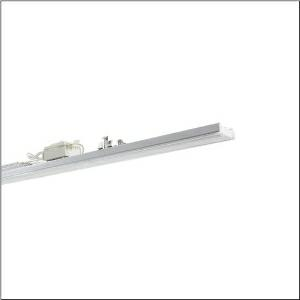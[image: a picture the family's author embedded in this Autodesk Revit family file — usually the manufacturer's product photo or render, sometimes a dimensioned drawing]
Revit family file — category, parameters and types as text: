
# Revit family: licross_r__21_recessed_mo_52tl12dn455g_fe02
name_source: partatom
category: Lighting Fixtures
units: mm (PartAtom-declared; Revit-internal decimal feet)

## family parameters
Cut with Voids When Loaded = No
Host = Face
Light Source = No
Part Type = Normal
Room Calculation Point = No
Round Connector Dimension = Use Diameter
Shared = No

## types (1)
- --- (1 x LED, 5500 lm, 29.6 W, 4000K)
    Apparent Load = 30 VA
    CIE Flux Codes = 72 92 99 100 100
    Color Rendering = 80
    Color Temperature = 4000K
    Default Elevation = 1800 mm
    Description = Licross® 21 Recessed MO, luminaire insert, of sheet steel, galvanised, coil coated, white, length: 1.500mm, width: 66mm, height: 67mm, LED rated luminous flux: 5.500lm, light colour: 840, control gear: DALI 2, with plug, 5-pole, with phase selection, mains connection: 220..240V, AC, 50/60Hz, rated input power: 30W, internal wiring halogen-free, primary optical cover: cover, of PMMA, light emission: direct distribution, primary light characteristic: symmetric, protection rating (complete): IP40, insulation class (complete): insulation class I (protective earthing), certification: CE, ENEC, VDE, UKCA, protection symbol: D if used in an environment without relevant dust loads with corresponding accessories, impact resistance: IK06, permissible ambient temperature for indoor applications: -25..+45°C, corresponds to IFS (International Featured Standards) requirements for safety and quality in the food industry, reducing of maximum allowable ambient temperature of 5°C with ceiling mounting, LABS conformity tested according to VDMA 24364:2018-05, packaging unit: 1 piece
    Height = 58 mm
    Lamp = 1 x LED
    Lamp Light Flux = 5500 lm
    Lamp Power = 29.6 W
    Lamp count = 1
    Length = 1500 mm
    Luminous efficacy = 186 lm/W
    Manufacturer = Siteco
    ModVariant = No
    Model = 52TL12DN455G
    Mounting Place = Ceiling
    Mounting Type = Pendant
    Number of Poles = 1
    OnlyDefault = Yes
    Power Factor = 1
    Product Name = Licross® 21 Recessed MO
    Product group = luminaire insert | ceiling pendant
    ProductGroupID = 902
    Protection Class = Protection class I
    Protection Degree = IP 40
    RLX_Detail_Level = 1
    RLX_Emergency_Light_Flux = 0 lm
    RLX_Emergency_Type = 0
    RLX_Emergency_Type_DB = No
    RlxData = <blob elided: 24037 chars, md5=a2fb8323>
    Socket = socket
    Standby Power = 0 W
    System Light Flux = 5500 lm
    System Power = 30 W
    Type Comments = factory setting: luminous flux: 100 % | dim-lin: 254 | 200 mA
    Type Image = l_1296930.jpg
    URL = http://relux.com
    VarID = @adj_147775
    Voltage = 0 V
    Weight = 0.00 kg
    Width = 66 mm

## geometry (parser evidence)
native form markers: Blend x4, Sweep x13
no freeform markers — native parametric forms only
